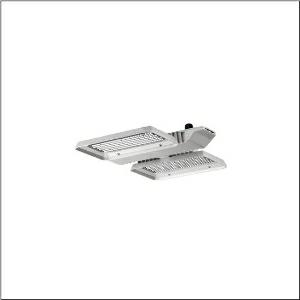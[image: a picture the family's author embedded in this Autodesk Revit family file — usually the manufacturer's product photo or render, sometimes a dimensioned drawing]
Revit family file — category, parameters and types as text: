
# Revit family: highbay_11_51hl62d14dca
name_source: partatom
category: Lighting Fixtures
units: mm (PartAtom-declared; Revit-internal decimal feet)

## family parameters
Cut with Voids When Loaded = No
Host = Face
Light Source = No
Part Type = Normal
Room Calculation Point = No
Round Connector Dimension = Use Diameter
Shared = No

## types (1)
- --- (1 x LED, 10020 lm, 55.6 W, 4000K)
    Apparent Load = 56 VA
    CIE Flux Codes = 89 96 99 100 100
    Color Rendering = 80
    Color Temperature = 4000K
    Default Elevation = 1800 mm
    Description = Highbay 11, LED high bay luminaire, primary light control with lens, of PMMA, light emission: direct distribution, primary light characteristic: symmetric, installation type: surface-mounted, suspended mounting, for 1x 2 x LED rated luminous flux: 10.020 lm, light colour: 840, colour temperature: 4000K, control gear: ECG DALI, with terminal, 5-pole, max. 2.5mm², mains connection: 230..240V, AC, 50/60Hz, rated input power: 56W, LED unit, of diecast aluminium, coated, metallic grey (RAL 9006), length: 470 mm, width: 500 mm, height: 65mm, housing, of diecast aluminium, coated, metallic grey (RAL 9006), protection rating (complete): IP65, insulation class (complete): insulation class I (protective earthing), certification: CE, ENEC, VDE, protection symbol: D, impact resistance: IK08 with glass or PC cover, permissible ambient temperature for indoor applications: -35..+70°C, corresponds to IFS (International Featured Standards) requirements for safety and quality in the food industry, reducing of maximum allowable ambient temperature of 5°C with ceiling mounting, packaging unit: 1 piece
    Height = 95 mm
    Lamp = 1 x LED
    Lamp Light Flux = 10020 lm
    Lamp Power = 55.6 W
    Lamp count = 1
    Length = 468 mm
    Luminous efficacy = 180 lm/W
    Manufacturer = Siteco
    ModVariant = No
    Model = 51HL62D14DCA
    Mounting Place = Ceiling
    Mounting Type = Pendant
    Number of Poles = 1
    OnlyDefault = Yes
    Power Factor = 1
    Product Name = Highbay 11
    Product group = LED high bay luminaire
    ProductGroupID = 903
    Protection Class = Protection class I
    Protection Degree = IP 65
    RLX_Detail_Level = 1
    RlxData = <blob elided: 70505 chars, md5=66ac0b94>
    Socket = socket
    Standby Power = 0 W
    System Light Flux = 10020 lm
    System Power = 56 W
    Type Comments = factory setting: luminous flux: 100 % | dim-lin: 254 | 315 mA
    Type Image = l_1003425.jpg
    URL = http://relux.com
    VarID = @adj_140821
    Voltage = 0 V
    Weight = 0.00 kg
    Width = 501 mm

## geometry (parser evidence)
native form markers: Blend x4, Sweep x12
no freeform markers — native parametric forms only
